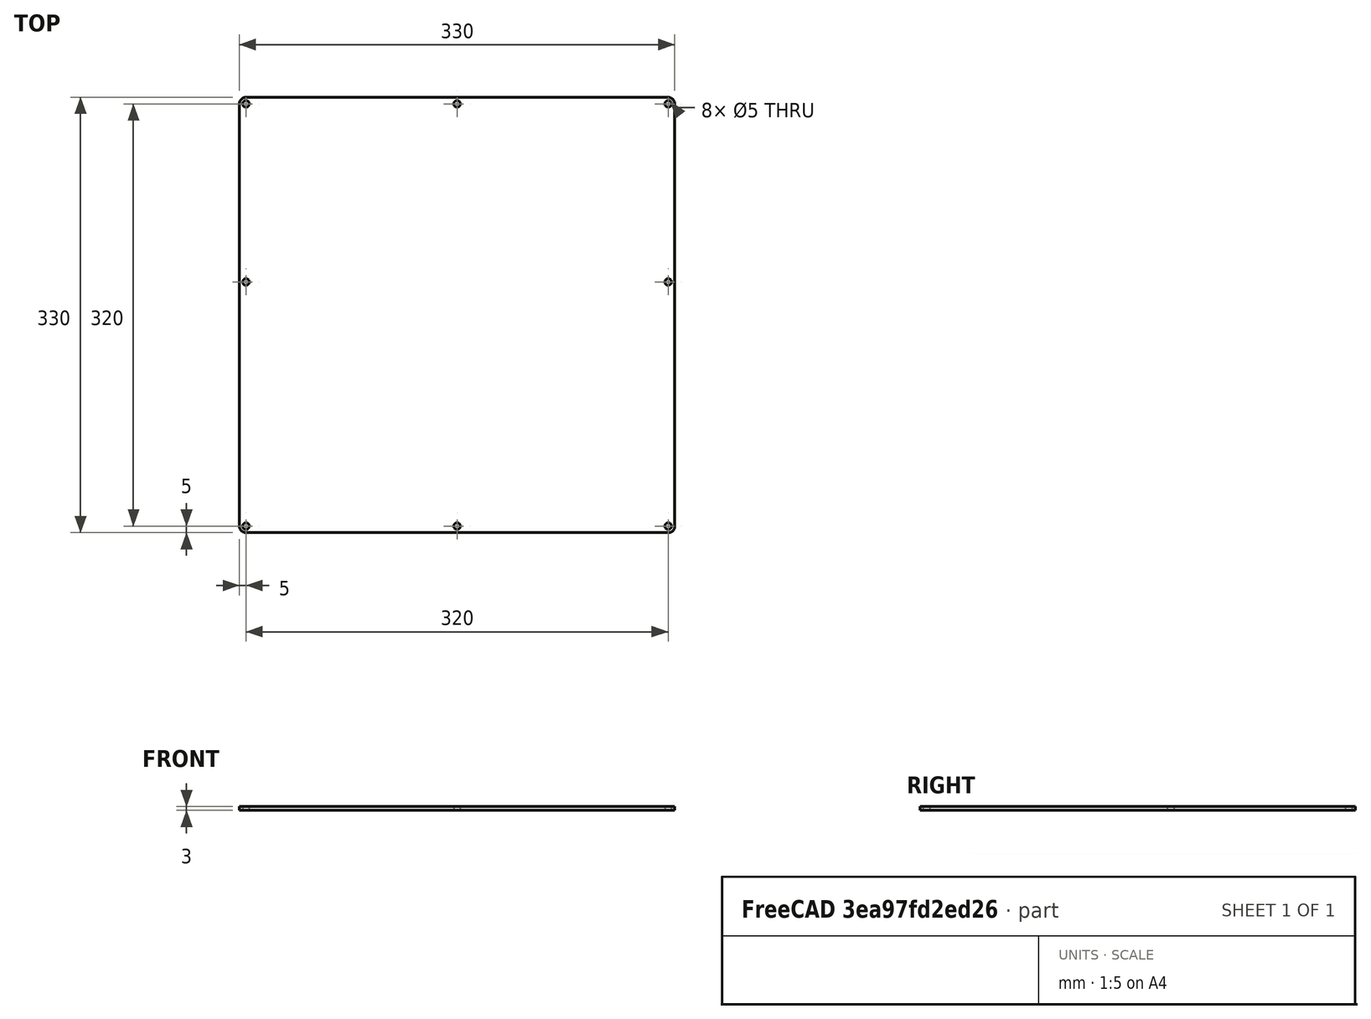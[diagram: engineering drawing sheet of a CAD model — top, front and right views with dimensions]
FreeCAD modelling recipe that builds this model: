
FCSTD DOCUMENT  (FreeCAD 0.20R25645 (Git))
Label: ALU MK2A
License: All rights reserved
LicenseURL: http://en.wikipedia.org/wiki/All_rights_reserved
objects: Sketcher::SketchObject×1, PartDesign::Pad×1, PartDesign::Body×1
note: 4 computed .brp shape members not serialized (recipe doc carries the construction recipe); baked Part::Feature solids carry a one-line shape summary decoded from their .brp

FEATURE [Sketcher::SketchObject] Sketch
  FullyConstrained = true
  MapMode = 5
  Support = -> [XY_Plane]
  sketch-geometry (24):
    g0: LineSegment StartX=-160 StartY=165 StartZ=0 EndX=160 EndY=165 EndZ=0
    g1: LineSegment StartX=165 StartY=160 StartZ=0 EndX=165 EndY=-160 EndZ=0
    g2: LineSegment StartX=160 StartY=-165 StartZ=0 EndX=-160 EndY=-165 EndZ=0
    g3: LineSegment StartX=-165 StartY=-160 StartZ=0 EndX=-165 EndY=160 EndZ=0
    g4: ArcOfCircle CenterX=-160 CenterY=160 CenterZ=0 NormalX=0 NormalY=0 NormalZ=1 AngleXU=0 Radius=5 StartAngle=1.5708 EndAngle=3.14159
    g5: GeomPoint X=-165 Y=165 Z=0
    g6: ArcOfCircle CenterX=160 CenterY=160 CenterZ=0 NormalX=0 NormalY=0 NormalZ=1 AngleXU=0 Radius=5 StartAngle=0 EndAngle=1.5708
    g7: GeomPoint X=165 Y=165 Z=0
    g8: ArcOfCircle CenterX=-160 CenterY=-160 CenterZ=0 NormalX=0 NormalY=0 NormalZ=1 AngleXU=0 Radius=5 StartAngle=3.14159 EndAngle=4.71239
    g9: GeomPoint X=-165 Y=-165 Z=0
    g10: ArcOfCircle CenterX=160 CenterY=-160 CenterZ=0 NormalX=0 NormalY=0 NormalZ=1 AngleXU=0 Radius=5 StartAngle=4.71239 EndAngle=6.28319
    g11: GeomPoint X=165 Y=-165 Z=0
    g12: Circle CenterX=-160 CenterY=160 CenterZ=0 NormalX=0 NormalY=0 NormalZ=1 AngleXU=0 Radius=2.5
    g13: Circle CenterX=160 CenterY=160 CenterZ=0 NormalX=0 NormalY=0 NormalZ=1 AngleXU=0 Radius=2.5
    g14: Circle CenterX=-160 CenterY=-160 CenterZ=0 NormalX=0 NormalY=0 NormalZ=1 AngleXU=0 Radius=2.5
    g15: Circle CenterX=160 CenterY=-160 CenterZ=0 NormalX=0 NormalY=0 NormalZ=1 AngleXU=0 Radius=2.5
    g16: LineSegment StartX=-160 StartY=-160 StartZ=0 EndX=160 EndY=-160 EndZ=0
    g17: LineSegment StartX=160 StartY=-160 StartZ=0 EndX=160 EndY=160 EndZ=0
    g18: LineSegment StartX=160 StartY=160 StartZ=0 EndX=-160 EndY=160 EndZ=0
    g19: LineSegment StartX=-160 StartY=160 StartZ=0 EndX=-160 EndY=-160 EndZ=0
    g20: Circle CenterX=0 CenterY=-160 CenterZ=0 NormalX=0 NormalY=0 NormalZ=1 AngleXU=0 Radius=2.5
    g21: Circle CenterX=0 CenterY=160 CenterZ=0 NormalX=0 NormalY=0 NormalZ=1 AngleXU=0 Radius=2.5
    g22: Circle CenterX=-160 CenterY=25 CenterZ=0 NormalX=0 NormalY=0 NormalZ=1 AngleXU=0 Radius=2.5
    g23: Circle CenterX=160 CenterY=25 CenterZ=0 NormalX=0 NormalY=0 NormalZ=1 AngleXU=0 Radius=2.5
  constraints (58):
    c: Horizontal(g0)
    c: Horizontal(g2)
    c: Vertical(g1)
    c: Vertical(g3)
    c: Symmetric(g5,g11,g-1)
    c: DistanceY(g9,g5) = 330
    c: DistanceX(g5,g7) = 330
    c: PointOnObject(g5,g3)
    c: PointOnObject(g5,g0)
    c: Tangent(g3,g4) = 1.5708
    c: Tangent(g0,g4) = 1.5708
    c: PointOnObject(g7,g1)
    c: PointOnObject(g7,g0)
    c: Tangent(g1,g6) = 1.5708
    c: Tangent(g0,g6) = 1.5708
    c: PointOnObject(g9,g2)
    c: PointOnObject(g9,g3)
    c: Tangent(g2,g8) = 1.5708
    c: Tangent(g3,g8) = 1.5708
    c: PointOnObject(g11,g2)
    c: PointOnObject(g11,g1)
    c: Tangent(g2,g10) = 1.5708
    c: Tangent(g1,g10) = 1.5708
    c: Equal(g8,g10)
    c: Equal(g10,g4)
    c: Equal(g4,g6)
    c: Radius(g6) = 5
    c: Coincident(g16,g17)
    c: Coincident(g17,g18)
    c: Coincident(g18,g19)
    c: Coincident(g19,g16)
    c: Horizontal(g16)
    c: Horizontal(g18)
    c: Vertical(g17)
    c: Vertical(g19)
    c: Coincident(g16,g14)
    c: Coincident(g17,g13)
    c: Coincident(g18,g12)
    c: Coincident(g16,g15)
    c: DistanceX(g16,g16) = 320
    c: Symmetric(g14,g13,g-1)
    c: DistanceY(g19,g19) = 320
    c: Equal(g14,g15)
    c: Equal(g15,g13)
    c: Equal(g13,g12)
    c: Radius(g12) = 2.5
    c: PointOnObject(g20,g-2)
    c: PointOnObject(g20,g16)
    c: Equal(g14,g20)
    c: PointOnObject(g21,g-2)
    c: PointOnObject(g21,g18)
    c: Equal(g12,g21)
    c: PointOnObject(g22,g19)
    c: DistanceY(g8,g22) = 185
    c: Equal(g14,g22)
    c: PointOnObject(g23,g17)
    c: Equal(g22,g23)
    c: Horizontal(g22,g23)
FEATURE [PartDesign::Pad] Pad
  Direction = (0,0,1)
  Length = 3
  Length2 = 100
  Profile = -> Sketch
  Type = 0
FEATURE [PartDesign::Body] Body
  Group = -> [Sketch,Pad]
  Origin = -> Origin
  Tip = -> Pad
